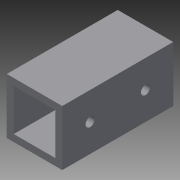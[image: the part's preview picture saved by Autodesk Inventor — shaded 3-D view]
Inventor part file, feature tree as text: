
AUTODESK INVENTOR PART (.ipt)
format: ipt  version: 2014 (Build 180170000, 170)  size: 90,112 bytes
history: native  units: in
note: dims shown in document units (in); Inventor stores cm internally (conversion verified against a paired STEP export)
features: extrude x2, sketch x2
ambient origin geometry x8: Origin, YZ Plane, XZ Plane, XY Plane, X Axis, Y Axis, Z Axis, Center Point
bodies: Solid1 (feature_tree)
feature tree (4):
  extrude  "Extrusion1"  Depth=1.0in
  extrude  "Extrusion2"  Depth=2.0in TaperAngle=0.0deg
  sketch  "Sketch1"  dims[d0=1.0in d1=1.0in]
  sketch  "Sketch2"  dims[d2=0.125in d3=2.0in d4=0.0in d5=0.163in d6=0.5in d7=0.5in d8=0.7874in d10=1.0in d11=0.3937in d13=1.0in d15=2.0in d16=0.0in]
